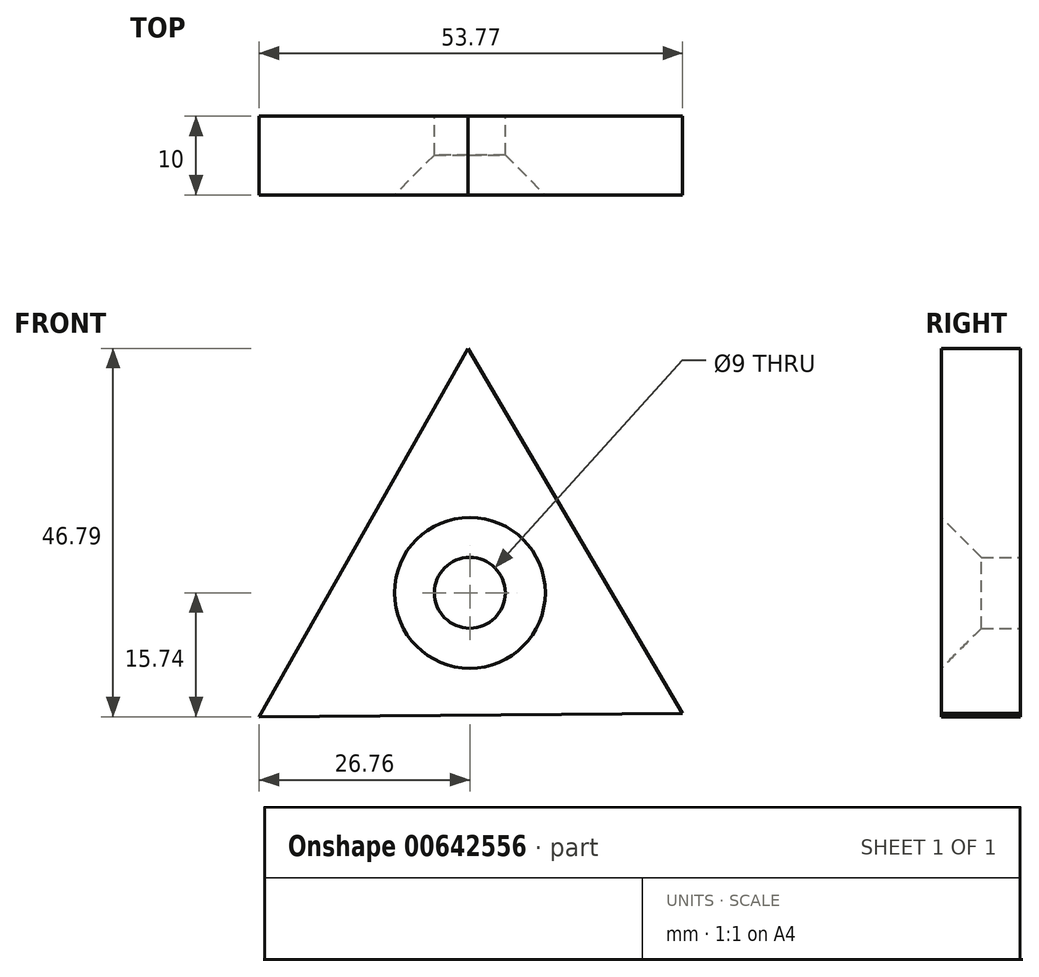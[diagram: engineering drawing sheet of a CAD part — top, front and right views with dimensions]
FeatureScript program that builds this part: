
annotation { "Feature Type Name" : "Feature", "Feature Type Description" : "" }
export const myFeature = defineFeature(function(context is Context, id is Id, definition is map)
    precondition{}
    {
        {
            var Q0;
            Q0=qCreatedBy(makeId("Front.planeOp"),FACE);
            var sketch = newSketch(context, id + "F0", { "sketchPlane" : qUnion([Q0])});
            skCircle(sketch, "E0", {"center": v(0, 0) * mm, "radius": 4.5 * mm});
            skCircle(sketch, "E1.cCircle", {"center": v(0, 0) * mm, "radius": 15.52 * mm, "construction": true});
            skLineSegment(sketch, "E1.0", {"start": v(-26.76, -15.74) * mm, "end": v(-0.25, 31.05) * mm});
            skLineSegment(sketch, "E1.1", {"start": v(-0.25, 31.05) * mm, "end": v(27.01, -15.3) * mm});
            skLineSegment(sketch, "E1.2", {"start": v(27.01, -15.3) * mm, "end": v(-26.76, -15.74) * mm});
            skPoint(sketch, "E1.0.midPoint", {"position": v(-13.5, 7.65) * mm});
            skSolve(sketch);
        }
        {
            var Q0;
            Q0=makeQuery(id+"F0.imprint","IMPRINT",FACE,{"disambiguationData":[TD([[makeQuery(id+"F0.imprint","IMPRINT",EDGE,{"derivedFrom":sQuery(id+"F0.wireOp",EDGE,"E0")}),-1.0]])]});
            extrude(context, id + "F1", {"entities" : qUnion([Q0]), "depth" : 10 * mm, "offsetDistance" : 25.4 * mm});
        }
        {
            var Q0;
            Q0=makeQuery(id+"F1.opExtrude","CAP_EDGE",EDGE,{"disambiguationData":[OSD([sQuery(id+"F0.wireOp",EDGE,"E0")])],"isStart":false});
            chamfer(context, id + "F2", {"entities" : qUnion([Q0]), "width" : 5.08 * mm, "tangentPropagation" : true});
        }
    });
